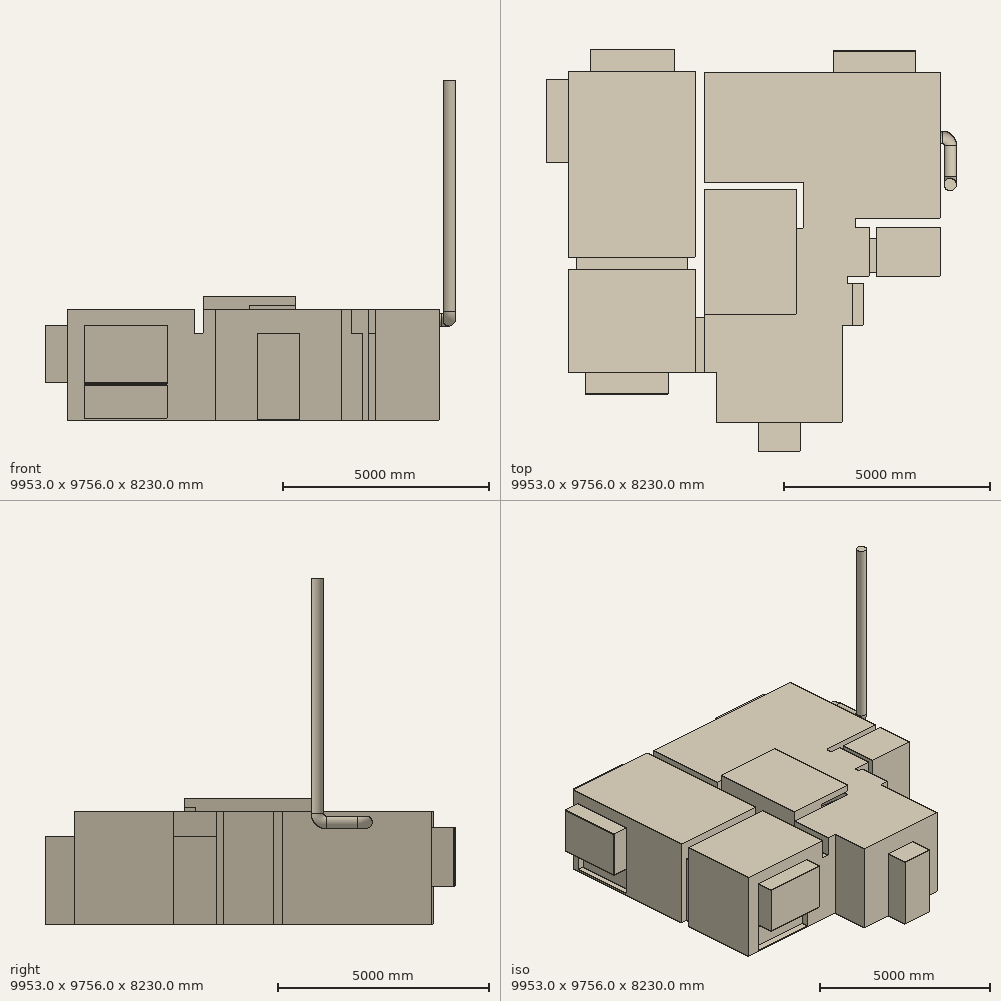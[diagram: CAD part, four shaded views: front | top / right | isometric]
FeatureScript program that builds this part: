
annotation { "Feature Type Name" : "Feature", "Feature Type Description" : "" }
export const myFeature = defineFeature(function(context is Context, id is Id, definition is map)
    precondition{}
    {
        {
            var Q0;
            Q0=qCreatedBy(makeId("Top.planeOp"),FACE);
            var sketch = newSketch(context, id + "F0", { "sketchPlane" : qUnion([Q0])});
            skLineSegment(sketch, "E0.bottom", {"start": v(-1549.14, 3434.73) * mm, "end": v(1546.86, 3434.73) * mm});
            skLineSegment(sketch, "E0.top", {"start": v(-1549.14, -1072.27) * mm, "end": v(1546.86, -1072.27) * mm});
            skLineSegment(sketch, "E0.left", {"start": v(-1549.14, 3434.73) * mm, "end": v(-1549.14, -1072.27) * mm});
            skLineSegment(sketch, "E0.right", {"start": v(1546.86, 3434.73) * mm, "end": v(1546.86, -1072.27) * mm});
            skSolve(sketch);
        }
        {
            var Q0;
            Q0=makeQuery(id+"F0.imprint","IMPRINT",FACE,{"disambiguationData":[TD([[makeQuery(id+"F0.imprint","IMPRINT",EDGE,{"derivedFrom":sQuery(id+"F0.wireOp",EDGE,"E0.bottom")}),-1.0]])]});
            extrude(context, id + "F1", {"entities" : qUnion([Q0]), "depth" : 2680 * mm});
        }
        {
            var Q0;
            Q0=makeQuery(id+"F1.opExtrude","SWEPT_FACE",FACE,{"disambiguationData":[OSD([sQuery(id+"F0.wireOp",EDGE,"E0.bottom")])]});
            var sketch = newSketch(context, id + "F2", { "sketchPlane" : qUnion([Q0])});
            skLineSegment(sketch, "E1.bottom", {"start": v(-1013.86, 2300) * mm, "end": v(1011.14, 2300) * mm});
            skLineSegment(sketch, "E1.top", {"start": v(-1013.86, 900) * mm, "end": v(1011.14, 900) * mm});
            skLineSegment(sketch, "E1.left", {"start": v(-1013.86, 2300) * mm, "end": v(-1013.86, 900) * mm});
            skLineSegment(sketch, "E1.right", {"start": v(1011.14, 2300) * mm, "end": v(1011.14, 900) * mm});
            skSolve(sketch);
        }
        {
            var Q0;
            Q0=qSketchRegion(id+"F2",true);
            extrude(context, id + "F3", {"entities" : qUnion([Q0]), "operationType" : NewBodyOperationType.ADD, "depth" : 532 * mm});
        }
        {
            var Q0;
            Q0=makeQuery(id+"F1.opExtrude","SWEPT_FACE",FACE,{"disambiguationData":[OSD([sQuery(id+"F0.wireOp",EDGE,"E0.left")])]});
            var sketch = newSketch(context, id + "F4", { "sketchPlane" : qUnion([Q0])});
            skLineSegment(sketch, "E2.bottom", {"start": v(-3238.73, 2300) * mm, "end": v(-1213.73, 2300) * mm});
            skLineSegment(sketch, "E2.top", {"start": v(-3238.73, 900) * mm, "end": v(-1213.73, 900) * mm});
            skLineSegment(sketch, "E2.left", {"start": v(-3238.73, 2300) * mm, "end": v(-3238.73, 900) * mm});
            skLineSegment(sketch, "E2.right", {"start": v(-1213.73, 2300) * mm, "end": v(-1213.73, 900) * mm});
            skSolve(sketch);
        }
        {
            var Q0;
            Q0=makeQuery(id+"F4.imprint","IMPRINT",FACE,{"disambiguationData":[TD([[makeQuery(id+"F4.imprint","IMPRINT",EDGE,{"derivedFrom":sQuery(id+"F4.wireOp",EDGE,"E2.bottom")}),-1.0]])]});
            extrude(context, id + "F5", {"entities" : qUnion([Q0]), "operationType" : NewBodyOperationType.ADD, "depth" : 532 * mm});
        }
        {
            var Q0;
            Q0=makeQuery(id+"F1.opExtrude","SWEPT_FACE",FACE,{"disambiguationData":[OSD([sQuery(id+"F0.wireOp",EDGE,"E0.bottom")])]});
            var sketch = newSketch(context, id + "F6", { "sketchPlane" : qUnion([Q0])});
            skLineSegment(sketch, "E3", {"start": v(1011.14, 900) * mm, "end": v(-1013.86, 900) * mm});
            skLineSegment(sketch, "E4.left", {"start": v(-1013.86, 835) * mm, "end": v(-1013.86, 35) * mm});
            skLineSegment(sketch, "E5.bottom", {"start": v(-1013.86, 835) * mm, "end": v(1011.14, 835) * mm});
            skLineSegment(sketch, "E5.top", {"start": v(-1013.86, 35) * mm, "end": v(1011.14, 35) * mm});
            skLineSegment(sketch, "E5.right", {"start": v(1011.14, 835) * mm, "end": v(1011.14, 35) * mm});
            skSolve(sketch);
        }
        {
            var Q0;
            Q0=makeQuery(id+"F6.imprint","IMPRINT",FACE,{"disambiguationData":[TD([[makeQuery(id+"F6.imprint","IMPRINT",EDGE,{"derivedFrom":sQuery(id+"F6.wireOp",EDGE,"E5.bottom")}),-1.0]])]});
            extrude(context, id + "F7", {"entities" : qUnion([Q0]), "operationType" : NewBodyOperationType.REMOVE, "oppositeDirection" : true, "depth" : 200 * mm});
        }
        {
            var Q0;
            Q0=makeQuery(id+"F1.opExtrude","CAP_FACE",FACE,{"disambiguationData":[OSD([sQuery(id+"F0.wireOp",EDGE,"E0.bottom"),sQuery(id+"F0.wireOp",EDGE,"E0.top"),sQuery(id+"F0.wireOp",EDGE,"E0.left"),sQuery(id+"F0.wireOp",EDGE,"E0.right")])],"isStart":true});
            var sketch = newSketch(context, id + "F8", { "sketchPlane" : qUnion([Q0])});
            skLineSegment(sketch, "E6", {"start": v(-1351.14, 1072.27) * mm, "end": v(-1351.14, 1375.27) * mm});
            skLineSegment(sketch, "E7", {"start": v(-1351.14, 1375.27) * mm, "end": v(1348.86, 1375.27) * mm});
            skLineSegment(sketch, "E8", {"start": v(1348.86, 1375.27) * mm, "end": v(1348.86, 1072.27) * mm});
            skLineSegment(sketch, "E9", {"start": v(1348.86, 1072.27) * mm, "end": v(-1351.14, 1072.27) * mm});
            skSolve(sketch);
        }
        {
            var Q0;
            Q0=makeQuery(id+"F8.imprint","IMPRINT",FACE,{"disambiguationData":[TD([[makeQuery(id+"F8.imprint","IMPRINT",EDGE,{"derivedFrom":sQuery(id+"F8.wireOp",EDGE,"E6")}),-1.0]])]});
            extrude(context, id + "F9", {"entities" : qUnion([Q0]), "operationType" : NewBodyOperationType.ADD, "oppositeDirection" : true, "depth" : 2100 * mm});
        }
        {
            var Q0;
            Q0=makeQuery(id+"F9.boolean.opBoolean","MERGE",FACE,{"derivedFrom":[makeQuery(id+"F1.opExtrude","CAP_FACE",FACE,{"disambiguationData":[OSD([sQuery(id+"F0.wireOp",EDGE,"E0.bottom"),sQuery(id+"F0.wireOp",EDGE,"E0.top"),sQuery(id+"F0.wireOp",EDGE,"E0.left"),sQuery(id+"F0.wireOp",EDGE,"E0.right")])],"isStart":true}),makeQuery(id+"F9.opExtrude","CAP_FACE",FACE,{"disambiguationData":[OSD([sQuery(id+"F8.wireOp",EDGE,"E6"),sQuery(id+"F8.wireOp",EDGE,"E7"),sQuery(id+"F8.wireOp",EDGE,"E8"),sQuery(id+"F8.wireOp",EDGE,"E9")])],"isStart":true})]});
            var sketch = newSketch(context, id + "F10", { "sketchPlane" : qUnion([Q0])});
            skLineSegment(sketch, "E10.bottom", {"start": v(-1549.14, 1375.27) * mm, "end": v(1546.86, 1375.27) * mm});
            skLineSegment(sketch, "E10.top", {"start": v(-1549.14, 3872.27) * mm, "end": v(1546.86, 3872.27) * mm});
            skLineSegment(sketch, "E10.left", {"start": v(-1549.14, 1375.27) * mm, "end": v(-1549.14, 3872.27) * mm});
            skLineSegment(sketch, "E10.right", {"start": v(1546.86, 1375.27) * mm, "end": v(1546.86, 3872.27) * mm});
            skLineSegment(sketch, "E11", {"start": v(-1549.14, 1375.27) * mm, "end": v(-1351.14, 1375.27) * mm});
            skSolve(sketch);
        }
        {
            var Q0;
            Q0=qSketchRegion(id+"F10",true);
            extrude(context, id + "F11", {"entities" : qUnion([Q0]), "operationType" : NewBodyOperationType.ADD, "oppositeDirection" : true, "depth" : 2680 * mm});
        }
        {
            var Q0;
            Q0=makeQuery(id+"F11.boolean.opBoolean","MERGE",FACE,{"derivedFrom":[makeQuery(id+"F9.boolean.opBoolean","MERGE",FACE,{"derivedFrom":[makeQuery(id+"F1.opExtrude","CAP_FACE",FACE,{"disambiguationData":[OSD([sQuery(id+"F0.wireOp",EDGE,"E0.bottom"),sQuery(id+"F0.wireOp",EDGE,"E0.top"),sQuery(id+"F0.wireOp",EDGE,"E0.left"),sQuery(id+"F0.wireOp",EDGE,"E0.right")])],"isStart":true}),makeQuery(id+"F9.opExtrude","CAP_FACE",FACE,{"disambiguationData":[OSD([sQuery(id+"F8.wireOp",EDGE,"E6"),sQuery(id+"F8.wireOp",EDGE,"E7"),sQuery(id+"F8.wireOp",EDGE,"E8"),sQuery(id+"F8.wireOp",EDGE,"E9")])],"isStart":true})]}),makeQuery(id+"F11.opExtrude","CAP_FACE",FACE,{"disambiguationData":[OSD([sQuery(id+"F10.wireOp",EDGE,"E10.bottom"),sQuery(id+"F10.wireOp",EDGE,"E10.top"),sQuery(id+"F10.wireOp",EDGE,"E10.left"),sQuery(id+"F10.wireOp",EDGE,"E10.right"),sQuery(id+"F10.wireOp",EDGE,"E11")])],"isStart":true})]});
            var sketch = newSketch(context, id + "F12", { "sketchPlane" : qUnion([Q0])});
            skLineSegment(sketch, "E12.bottom", {"start": v(1546.86, 3872.27) * mm, "end": v(1765.86, 3872.27) * mm});
            skLineSegment(sketch, "E12.top", {"start": v(1546.86, 2526.27) * mm, "end": v(1765.86, 2526.27) * mm});
            skLineSegment(sketch, "E12.left", {"start": v(1546.86, 3872.27) * mm, "end": v(1546.86, 2526.27) * mm});
            skLineSegment(sketch, "E12.right", {"start": v(1765.86, 3872.27) * mm, "end": v(1765.86, 2526.27) * mm});
            skSolve(sketch);
        }
        {
            var Q0;
            Q0=makeQuery(id+"F12.imprint","IMPRINT",FACE,{"disambiguationData":[TD([[makeQuery(id+"F12.imprint","IMPRINT",EDGE,{"derivedFrom":sQuery(id+"F12.wireOp",EDGE,"E12.bottom")}),-1.0]])]});
            extrude(context, id + "F13", {"entities" : qUnion([Q0]), "operationType" : NewBodyOperationType.ADD, "oppositeDirection" : true, "depth" : 2100 * mm});
        }
        {
            var Q0;
            Q0=makeQuery(id+"F13.boolean.opBoolean","MERGE",FACE,{"derivedFrom":[makeQuery(id+"F11.opExtrude","SWEPT_FACE",FACE,{"disambiguationData":[OSD([sQuery(id+"F10.wireOp",EDGE,"E10.top")])]}),makeQuery(id+"F13.opExtrude","SWEPT_FACE",FACE,{"disambiguationData":[OSD([sQuery(id+"F12.wireOp",EDGE,"E12.bottom")])]})]});
            var sketch = newSketch(context, id + "F14", { "sketchPlane" : qUnion([Q0])});
            skLineSegment(sketch, "E13.bottom", {"start": v(-1134.15, 2296.53) * mm, "end": v(890.85, 2296.53) * mm});
            skLineSegment(sketch, "E13.top", {"start": v(-1134.15, 896.53) * mm, "end": v(890.85, 896.53) * mm});
            skLineSegment(sketch, "E13.left", {"start": v(-1134.15, 2296.53) * mm, "end": v(-1134.15, 896.53) * mm});
            skLineSegment(sketch, "E13.right", {"start": v(890.85, 2296.53) * mm, "end": v(890.85, 896.53) * mm});
            skSolve(sketch);
        }
        {
            var Q0;
            Q0=makeQuery(id+"F14.imprint","IMPRINT",FACE,{"disambiguationData":[TD([[makeQuery(id+"F14.imprint","IMPRINT",EDGE,{"derivedFrom":sQuery(id+"F14.wireOp",EDGE,"E13.bottom")}),-1.0]])]});
            extrude(context, id + "F15", {"entities" : qUnion([Q0]), "operationType" : NewBodyOperationType.ADD, "depth" : 532 * mm});
        }
        {
            var Q0;
            Q0=makeQuery(id+"F12.imprint","IMPRINT",FACE,{"disambiguationData":[TD([[makeQuery(id+"F12.imprint","IMPRINT",EDGE,{"derivedFrom":sQuery(id+"F12.wireOp",EDGE,"E12.bottom")}),-1.0]])]});
            var sketch = newSketch(context, id + "F16", { "sketchPlane" : qUnion([Q0])});
            skLineSegment(sketch, "E14", {"start": v(1765.86, 3872.27) * mm, "end": v(2057.86, 3872.27) * mm});
            skLineSegment(sketch, "E15", {"start": v(2057.86, 3872.27) * mm, "end": v(2057.86, 5091.27) * mm});
            skLineSegment(sketch, "E16", {"start": v(1765.86, 3872.27) * mm, "end": v(1765.86, 2474.27) * mm});
            skLineSegment(sketch, "E17", {"start": v(1765.86, 2474.27) * mm, "end": v(2915.86, 2474.27) * mm});
            skLineSegment(sketch, "E18", {"start": v(2915.86, 2474.27) * mm, "end": v(2915.86, 2739.27) * mm});
            skLineSegment(sketch, "E19", {"start": v(2915.86, 2739.27) * mm, "end": v(5096.86, 2739.27) * mm});
            skLineSegment(sketch, "E20", {"start": v(5096.86, 2739.27) * mm, "end": v(5096.86, 5091.27) * mm});
            skLineSegment(sketch, "E21", {"start": v(2057.86, 5091.27) * mm, "end": v(5096.86, 5091.27) * mm});
            skSolve(sketch);
        }
        {
            var Q0;
            {var subQ1=sQuery(id+"F16.wireOp",EDGE,"E14");Q0=makeQuery(id+"F16.imprint","IMPRINT",FACE,{"disambiguationData":[TD([[makeQuery(id+"F16.imprint","IMPRINT",EDGE,{"derivedFrom":subQ1}),-1.0]])]});}
            extrude(context, id + "F17", {"entities" : qUnion([Q0]), "operationType" : NewBodyOperationType.ADD, "oppositeDirection" : true, "depth" : 2680 * mm});
        }
        {
            var Q0;
            Q0=makeQuery(id+"F17.boolean.opBoolean","MERGE",FACE,{"derivedFrom":[makeQuery(id+"F13.boolean.opBoolean","MERGE",FACE,{"derivedFrom":[makeQuery(id+"F11.boolean.opBoolean","MERGE",FACE,{"derivedFrom":[makeQuery(id+"F9.boolean.opBoolean","MERGE",FACE,{"derivedFrom":[makeQuery(id+"F1.opExtrude","CAP_FACE",FACE,{"disambiguationData":[OSD([sQuery(id+"F0.wireOp",EDGE,"E0.bottom"),sQuery(id+"F0.wireOp",EDGE,"E0.top"),sQuery(id+"F0.wireOp",EDGE,"E0.left"),sQuery(id+"F0.wireOp",EDGE,"E0.right")])],"isStart":true}),makeQuery(id+"F9.opExtrude","CAP_FACE",FACE,{"disambiguationData":[OSD([sQuery(id+"F8.wireOp",EDGE,"E6"),sQuery(id+"F8.wireOp",EDGE,"E7"),sQuery(id+"F8.wireOp",EDGE,"E8"),sQuery(id+"F8.wireOp",EDGE,"E9")])],"isStart":true})]}),makeQuery(id+"F11.opExtrude","CAP_FACE",FACE,{"disambiguationData":[OSD([sQuery(id+"F10.wireOp",EDGE,"E10.bottom"),sQuery(id+"F10.wireOp",EDGE,"E10.top"),sQuery(id+"F10.wireOp",EDGE,"E10.left"),sQuery(id+"F10.wireOp",EDGE,"E10.right"),sQuery(id+"F10.wireOp",EDGE,"E11")])],"isStart":true})]}),makeQuery(id+"F13.opExtrude","CAP_FACE",FACE,{"disambiguationData":[OSD([sQuery(id+"F12.wireOp",EDGE,"E12.bottom"),sQuery(id+"F12.wireOp",EDGE,"E12.top"),sQuery(id+"F12.wireOp",EDGE,"E12.left"),sQuery(id+"F12.wireOp",EDGE,"E12.right")])],"isStart":true})]}),makeQuery(id+"F17.opExtrude","CAP_FACE",FACE,{"disambiguationData":[OSD([sQuery(id+"F16.wireOp",EDGE,"E14"),sQuery(id+"F16.wireOp",EDGE,"E15"),sQuery(id+"F16.wireOp",EDGE,"E16"),sQuery(id+"F16.wireOp",EDGE,"E17"),sQuery(id+"F16.wireOp",EDGE,"E18"),sQuery(id+"F16.wireOp",EDGE,"E19"),sQuery(id+"F16.wireOp",EDGE,"E20"),sQuery(id+"F16.wireOp",EDGE,"E21")])],"isStart":true})]});
            var sketch = newSketch(context, id + "F18", { "sketchPlane" : qUnion([Q0])});
            skLineSegment(sketch, "E22.bottom", {"start": v(3064.86, 5091.27) * mm, "end": v(4089.86, 5091.27) * mm});
            skLineSegment(sketch, "E22.top", {"start": v(3064.86, 5789.27) * mm, "end": v(4089.86, 5789.27) * mm});
            skLineSegment(sketch, "E22.left", {"start": v(3064.86, 5091.27) * mm, "end": v(3064.86, 5789.27) * mm});
            skLineSegment(sketch, "E22.right", {"start": v(4089.86, 5091.27) * mm, "end": v(4089.86, 5789.27) * mm});
            skSolve(sketch);
        }
        {
            var Q0;
            Q0=makeQuery(id+"F18.imprint","IMPRINT",FACE,{"disambiguationData":[TD([[makeQuery(id+"F18.imprint","IMPRINT",EDGE,{"derivedFrom":sQuery(id+"F18.wireOp",EDGE,"E22.bottom")}),1.0]])]});
            extrude(context, id + "F19", {"entities" : qUnion([Q0]), "operationType" : NewBodyOperationType.ADD, "oppositeDirection" : true, "depth" : 2100 * mm});
        }
        {
            var Q0;
            {var subQ0=sQuery(id+"F16.wireOp",EDGE,"E14");Q0=makeQuery(id+"F16.imprint","IMPRINT",FACE,{"disambiguationData":[TD([[makeQuery(id+"F16.imprint","IMPRINT",EDGE,{"derivedFrom":subQ0}),-1.0]])]});}
            var sketch = newSketch(context, id + "F20", { "sketchPlane" : qUnion([Q0])});
            skLineSegment(sketch, "E23.bottom", {"start": v(1765.86, 2474.27) * mm, "end": v(3985.86, 2474.27) * mm});
            skLineSegment(sketch, "E23.top", {"start": v(1765.86, -565.73) * mm, "end": v(3985.86, -565.73) * mm});
            skLineSegment(sketch, "E23.left", {"start": v(1765.86, 2474.27) * mm, "end": v(1765.86, -565.73) * mm});
            skLineSegment(sketch, "E23.right", {"start": v(3985.86, 2474.27) * mm, "end": v(3985.86, -565.73) * mm});
            skSolve(sketch);
        }
        {
            var Q0;
            Q0=makeQuery(id+"F20.imprint","IMPRINT",FACE,{"disambiguationData":[TD([[makeQuery(id+"F20.imprint","IMPRINT",EDGE,{"derivedFrom":sQuery(id+"F20.wireOp",EDGE,"E23.top")}),1.0]])]});
            extrude(context, id + "F21", {"entities" : qUnion([Q0]), "oppositeDirection" : true, "depth" : 3000 * mm});
        }
        {
            var Q0;
            Q0=makeQuery(id+"F21.opExtrude","SWEPT_FACE",FACE,{"disambiguationData":[OSD([sQuery(id+"F20.wireOp",EDGE,"E23.left")])]});
            var sketch = newSketch(context, id + "F22", { "sketchPlane" : qUnion([Q0])});
            skLineSegment(sketch, "E24.MirrorCS", {"start": v(1199.27, 1020) * mm, "end": v(944.27, 1020) * mm});
            skLineSegment(sketch, "E25.MirrorCS", {"start": v(1709.27, 680) * mm, "end": v(1454.27, 680) * mm});
            skLineSegment(sketch, "E26.MirrorCS", {"start": v(2219.27, 340) * mm, "end": v(1964.27, 340) * mm});
            skLineSegment(sketch, "E27.MirrorCS", {"start": v(2474.27, 0) * mm, "end": v(2219.27, 0) * mm});
            skLineSegment(sketch, "E28.MirrorCS", {"start": v(1964.27, 340) * mm, "end": v(1964.27, 510) * mm});
            skLineSegment(sketch, "E29.MirrorCS", {"start": v(1454.27, 680) * mm, "end": v(1454.27, 850) * mm});
            skLineSegment(sketch, "E30.MirrorCS", {"start": v(1709.27, 510) * mm, "end": v(1709.27, 680) * mm});
            skLineSegment(sketch, "E31.MirrorCS", {"start": v(1199.27, 850) * mm, "end": v(1199.27, 1020) * mm});
            skLineSegment(sketch, "E32.MirrorCS", {"start": v(1454.27, 850) * mm, "end": v(1199.27, 850) * mm});
            skLineSegment(sketch, "E33.MirrorCS", {"start": v(-565.73, 1530) * mm, "end": v(-565.73, 1330) * mm});
            skLineSegment(sketch, "E34.MirrorCS", {"start": v(2219.27, 170) * mm, "end": v(2219.27, 340) * mm});
            skLineSegment(sketch, "E35.MirrorCS", {"start": v(2474.27, 170) * mm, "end": v(2219.27, 170) * mm});
            skLineSegment(sketch, "E36.MirrorCS", {"start": v(1964.27, 510) * mm, "end": v(1709.27, 510) * mm});
            skLineSegment(sketch, "E37.MirrorCS", {"start": v(2474.27, 0) * mm, "end": v(2474.27, 170) * mm});
            skLineSegment(sketch, "E38.MirrorCS", {"start": v(2474.27, 170) * mm, "end": v(2474.27, 0) * mm});
            skLineSegment(sketch, "E39", {"start": v(2219.27, 0) * mm, "end": v(179.27, 1330) * mm});
            skLineSegment(sketch, "E40", {"start": v(944.27, 1020) * mm, "end": v(944.27, 1190) * mm});
            skLineSegment(sketch, "E41", {"start": v(944.27, 1190) * mm, "end": v(689.27, 1190) * mm});
            skLineSegment(sketch, "E42", {"start": v(689.27, 1190) * mm, "end": v(689.27, 1330) * mm});
            skLineSegment(sketch, "E43", {"start": v(689.27, 1330) * mm, "end": v(434.27, 1330) * mm});
            skLineSegment(sketch, "E44", {"start": v(434.27, 1330) * mm, "end": v(434.27, 1530) * mm});
            skLineSegment(sketch, "E45", {"start": v(434.27, 1530) * mm, "end": v(-565.73, 1530) * mm});
            skLineSegment(sketch, "E46", {"start": v(-565.73, 1330) * mm, "end": v(179.27, 1330) * mm});
            skSolve(sketch);
        }
        {
            var Q0;
            Q0=qSketchRegion(id+"F22",true);
            extrude(context, id + "F23", {"entities" : qUnion([Q0]), "operationType" : NewBodyOperationType.REMOVE, "oppositeDirection" : true, "depth" : 1110 * mm});
        }
        {
            var Q0;
            Q0=makeQuery(id+"F21.opExtrude","SWEPT_FACE",FACE,{"disambiguationData":[OSD([sQuery(id+"F20.wireOp",EDGE,"E23.right")])]});
            var sketch = newSketch(context, id + "F24", { "sketchPlane" : qUnion([Q0])});
            skLineSegment(sketch, "E47", {"start": v(565.73, 1530) * mm, "end": v(-689.27, 1530) * mm});
            skLineSegment(sketch, "E48", {"start": v(-689.27, 1530) * mm, "end": v(-689.27, 1710) * mm});
            skLineSegment(sketch, "E49", {"start": v(-689.27, 1710) * mm, "end": v(-944.27, 1710) * mm});
            skLineSegment(sketch, "E50", {"start": v(-944.27, 1710) * mm, "end": v(-944.27, 1890) * mm});
            skLineSegment(sketch, "E51", {"start": v(-944.27, 1890) * mm, "end": v(-1199.27, 1890) * mm});
            skLineSegment(sketch, "E52", {"start": v(-1199.27, 1890) * mm, "end": v(-1199.27, 2070) * mm});
            skLineSegment(sketch, "E53", {"start": v(-1199.27, 2070) * mm, "end": v(-1454.27, 2070) * mm});
            skLineSegment(sketch, "E54", {"start": v(-1454.27, 2070) * mm, "end": v(-1454.27, 2250) * mm});
            skLineSegment(sketch, "E55", {"start": v(-1454.27, 2250) * mm, "end": v(-1709.27, 2250) * mm});
            skLineSegment(sketch, "E56", {"start": v(-1709.27, 2430) * mm, "end": v(-1709.27, 2250) * mm});
            skLineSegment(sketch, "E57", {"start": v(565.73, 1530) * mm, "end": v(565.73, 1330) * mm});
            skLineSegment(sketch, "E58", {"start": v(-689.27, 1330) * mm, "end": v(565.73, 1330) * mm});
            skLineSegment(sketch, "E59", {"start": v(-1709.27, 2430) * mm, "end": v(-1964.27, 2430) * mm});
            skLineSegment(sketch, "E60", {"start": v(-1964.27, 2430) * mm, "end": v(-1964.27, 2610) * mm});
            skLineSegment(sketch, "E61", {"start": v(-1964.27, 2610) * mm, "end": v(-2219.27, 2610) * mm});
            skLineSegment(sketch, "E62", {"start": v(-2219.27, 2610) * mm, "end": v(-2219.27, 2790) * mm});
            skLineSegment(sketch, "E63", {"start": v(-2219.27, 2790) * mm, "end": v(-2474.27, 2790) * mm});
            skLineSegment(sketch, "E64", {"start": v(-2474.27, 2651.89) * mm, "end": v(-689.27, 1330) * mm});
            skLineSegment(sketch, "E65", {"start": v(-2474.27, 2651.89) * mm, "end": v(-2474.27, 2790) * mm});
            skLineSegment(sketch, "E66", {"start": v(565.73, 1330) * mm, "end": v(565.73, 1530) * mm});
            skLineSegment(sketch, "E67", {"start": v(-689.27, 1530) * mm, "end": v(565.73, 1530) * mm});
            skSolve(sketch);
        }
        {
            var Q0;
            Q0=makeQuery(id+"F24.imprint","IMPRINT",FACE,{"disambiguationData":[TD([[makeQuery(id+"F24.imprint","IMPRINT",EDGE,{"derivedFrom":sQuery(id+"F24.wireOp",EDGE,"E48")}),1.0]])]});
            extrude(context, id + "F25", {"entities" : qUnion([Q0]), "operationType" : NewBodyOperationType.REMOVE, "oppositeDirection" : true, "depth" : 1120 * mm});
        }
        {
            var Q0;
            Q0=makeQuery(id+"F17.opExtrude","CAP_FACE",FACE,{"disambiguationData":[OSD([sQuery(id+"F16.wireOp",EDGE,"E14"),sQuery(id+"F16.wireOp",EDGE,"E15"),sQuery(id+"F16.wireOp",EDGE,"E16"),sQuery(id+"F16.wireOp",EDGE,"E17"),sQuery(id+"F16.wireOp",EDGE,"E18"),sQuery(id+"F16.wireOp",EDGE,"E19"),sQuery(id+"F16.wireOp",EDGE,"E20"),sQuery(id+"F16.wireOp",EDGE,"E21")])],"isStart":false});
            var sketch = newSketch(context, id + "F26", { "sketchPlane" : qUnion([Q0])});
            skLineSegment(sketch, "E68", {"start": v(5096.86, -2739.27) * mm, "end": v(5356.86, -2739.27) * mm});
            skLineSegment(sketch, "E69", {"start": v(5221.86, -1714.27) * mm, "end": v(5221.86, -1554.27) * mm});
            skLineSegment(sketch, "E70", {"start": v(5221.86, -1554.27) * mm, "end": v(5771.86, -1554.27) * mm});
            skLineSegment(sketch, "E71", {"start": v(5771.86, -1554.27) * mm, "end": v(5771.86, -1454.27) * mm});
            skLineSegment(sketch, "E72", {"start": v(5771.86, -629.27) * mm, "end": v(5771.86, -354.27) * mm});
            skLineSegment(sketch, "E73", {"start": v(5771.86, -354.27) * mm, "end": v(5421.86, -354.27) * mm});
            skLineSegment(sketch, "E74", {"start": v(5421.86, -354.27) * mm, "end": v(5421.86, -142.27) * mm});
            skLineSegment(sketch, "E75", {"start": v(7471.86, 3404.73) * mm, "end": v(6893.86, 3404.73) * mm});
            skLineSegment(sketch, "E76", {"start": v(4681.86, 3404.73) * mm, "end": v(1765.86, 3404.73) * mm});
            skLineSegment(sketch, "E77", {"start": v(1765.86, 3404.73) * mm, "end": v(1765.86, 747.73) * mm});
            skLineSegment(sketch, "E78", {"start": v(1765.86, 747.73) * mm, "end": v(4146.86, 747.73) * mm});
            skLineSegment(sketch, "E79", {"start": v(4146.86, 747.73) * mm, "end": v(4146.86, -384.27) * mm});
            skLineSegment(sketch, "E80", {"start": v(5096.86, -2739.27) * mm, "end": v(2915.86, -2739.27) * mm});
            skLineSegment(sketch, "E81", {"start": v(2915.86, -2739.27) * mm, "end": v(2915.86, -2474.27) * mm});
            skLineSegment(sketch, "E82", {"start": v(2915.86, -2474.27) * mm, "end": v(3985.86, -2474.27) * mm});
            skLineSegment(sketch, "E83", {"start": v(3985.86, -2474.27) * mm, "end": v(3985.86, -384.27) * mm});
            skLineSegment(sketch, "E84", {"start": v(3985.86, -384.27) * mm, "end": v(4146.86, -384.27) * mm});
            skLineSegment(sketch, "E85", {"start": v(5771.86, -629.27) * mm, "end": v(5771.86, -1454.27) * mm});
            skLineSegment(sketch, "E86", {"start": v(4681.86, 3404.73) * mm, "end": v(6893.86, 3404.73) * mm});
            skLineSegment(sketch, "E87", {"start": v(5356.86, -2739.27) * mm, "end": v(5356.86, -1714.27) * mm});
            skLineSegment(sketch, "E88", {"start": v(5356.86, -1714.27) * mm, "end": v(5221.86, -1714.27) * mm});
            skLineSegment(sketch, "E89", {"start": v(7471.86, 3404.73) * mm, "end": v(7471.86, -142.27) * mm});
            skLineSegment(sketch, "E90", {"start": v(5421.86, -142.27) * mm, "end": v(7471.86, -142.27) * mm});
            skSolve(sketch);
        }
        {
            var Q0;
            Q0=makeQuery(id+"F26.imprint","IMPRINT",FACE,{"disambiguationData":[TD([[makeQuery(id+"F26.imprint","IMPRINT",EDGE,{"derivedFrom":sQuery(id+"F26.wireOp",EDGE,"E68")}),1.0]])]});
            extrude(context, id + "F27", {"entities" : qUnion([Q0]), "oppositeDirection" : true, "depth" : 2680 * mm});
        }
        {
            var Q0;
            Q0=makeQuery(id+"F27.opExtrude","SWEPT_FACE",FACE,{"disambiguationData":[OSD([sQuery(id+"F26.wireOp",EDGE,"E75"),sQuery(id+"F26.wireOp",EDGE,"E76"),sQuery(id+"F26.wireOp",EDGE,"E86")])]});
            var sketch = newSketch(context, id + "F28", { "sketchPlane" : qUnion([Q0])});
            skLineSegment(sketch, "E91.bottom", {"start": v(-6883.86, 2300) * mm, "end": v(-4883.86, 2300) * mm});
            skLineSegment(sketch, "E91.top", {"start": v(-6883.86, 900) * mm, "end": v(-4883.86, 900) * mm});
            skLineSegment(sketch, "E91.left", {"start": v(-6883.86, 2300) * mm, "end": v(-6883.86, 900) * mm});
            skLineSegment(sketch, "E91.right", {"start": v(-4883.86, 2300) * mm, "end": v(-4883.86, 900) * mm});
            skSolve(sketch);
        }
        {
            var Q0;
            Q0=makeQuery(id+"F28.imprint","IMPRINT",FACE,{"disambiguationData":[TD([[makeQuery(id+"F28.imprint","IMPRINT",EDGE,{"derivedFrom":sQuery(id+"F28.wireOp",EDGE,"E91.bottom")}),-1.0]])]});
            extrude(context, id + "F29", {"entities" : qUnion([Q0]), "operationType" : NewBodyOperationType.ADD, "depth" : 532 * mm});
        }
        {
            var Q0;
            Q0=makeQuery(id+"F27.opExtrude","SWEPT_FACE",FACE,{"disambiguationData":[OSD([sQuery(id+"F26.wireOp",EDGE,"E71"),sQuery(id+"F26.wireOp",EDGE,"E72"),sQuery(id+"F26.wireOp",EDGE,"E85")])]});
            var sketch = newSketch(context, id + "F30", { "sketchPlane" : qUnion([Q0])});
            skLineSegment(sketch, "E92.bottom", {"start": v(-1454.27, 2100) * mm, "end": v(-629.27, 2100) * mm});
            skLineSegment(sketch, "E92.top", {"start": v(-1454.27, 0) * mm, "end": v(-629.27, 0) * mm});
            skLineSegment(sketch, "E92.left", {"start": v(-1454.27, 2100) * mm, "end": v(-1454.27, 0) * mm});
            skLineSegment(sketch, "E92.right", {"start": v(-629.27, 2100) * mm, "end": v(-629.27, 0) * mm});
            skSolve(sketch);
        }
        {
            var Q0;
            Q0=makeQuery(id+"F30.imprint","IMPRINT",FACE,{"disambiguationData":[TD([[makeQuery(id+"F30.imprint","IMPRINT",EDGE,{"derivedFrom":sQuery(id+"F30.wireOp",EDGE,"E92.bottom")}),-1.0]])]});
            extrude(context, id + "F31", {"entities" : qUnion([Q0]), "operationType" : NewBodyOperationType.ADD, "depth" : 160 * mm});
        }
        {
            var Q0;
            Q0=makeQuery(id+"F31.opExtrude","CAP_FACE",FACE,{"disambiguationData":[OSD([sQuery(id+"F30.wireOp",EDGE,"E92.bottom"),sQuery(id+"F30.wireOp",EDGE,"E92.top"),sQuery(id+"F30.wireOp",EDGE,"E92.left"),sQuery(id+"F30.wireOp",EDGE,"E92.right")])],"isStart":false});
            var sketch = newSketch(context, id + "F32", { "sketchPlane" : qUnion([Q0])});
            skLineSegment(sketch, "E93.bottom", {"start": v(-1554.27, 2680) * mm, "end": v(-354.27, 2680) * mm});
            skLineSegment(sketch, "E93.top", {"start": v(-1554.27, 0) * mm, "end": v(-354.27, 0) * mm});
            skLineSegment(sketch, "E93.left", {"start": v(-1554.27, 2680) * mm, "end": v(-1554.27, 0) * mm});
            skLineSegment(sketch, "E93.right", {"start": v(-354.27, 2680) * mm, "end": v(-354.27, 0) * mm});
            skSolve(sketch);
        }
        {
            var Q0;
            Q0=qSketchRegion(id+"F32",true);
            extrude(context, id + "F33", {"entities" : qUnion([Q0]), "operationType" : NewBodyOperationType.ADD, "depth" : 1540 * mm});
        }
        {
            var Q0;
            Q0=makeQuery(id+"F1.opExtrude","SWEPT_BODY",BODY,{"disambiguationData":[OSD([sQuery(id+"F0.wireOp",EDGE,"E0.bottom"),sQuery(id+"F0.wireOp",EDGE,"E0.top"),sQuery(id+"F0.wireOp",EDGE,"E0.left"),sQuery(id+"F0.wireOp",EDGE,"E0.right")])]});
            var Q1;
            Q1=makeQuery(id+"F27.opExtrude","SWEPT_BODY",BODY,{"disambiguationData":[OSD([sQuery(id+"F26.wireOp",EDGE,"E68"),sQuery(id+"F26.wireOp",EDGE,"f08b4c50-08dc-44d1-91bd-df31dd3f817a"),sQuery(id+"F26.wireOp",EDGE,"f896f5a7-1bc8-498b-a9e9-afe6711b9f40"),sQuery(id+"F26.wireOp",EDGE,"E69"),sQuery(id+"F26.wireOp",EDGE,"E70"),sQuery(id+"F26.wireOp",EDGE,"E71"),sQuery(id+"F26.wireOp",EDGE,"E72"),sQuery(id+"F26.wireOp",EDGE,"E73"),sQuery(id+"F26.wireOp",EDGE,"E74"),sQuery(id+"F26.wireOp",EDGE,"4dea9934-df3e-44db-ac8b-cfe9eaf94726"),sQuery(id+"F26.wireOp",EDGE,"69e68077-ab11-4f7d-8ed4-810636c2d2b1"),sQuery(id+"F26.wireOp",EDGE,"E75"),sQuery(id+"F26.wireOp",EDGE,"E76"),sQuery(id+"F26.wireOp",EDGE,"E77"),sQuery(id+"F26.wireOp",EDGE,"E78"),sQuery(id+"F26.wireOp",EDGE,"E79"),sQuery(id+"F26.wireOp",EDGE,"E80"),sQuery(id+"F26.wireOp",EDGE,"E81"),sQuery(id+"F26.wireOp",EDGE,"E82"),sQuery(id+"F26.wireOp",EDGE,"E83"),sQuery(id+"F26.wireOp",EDGE,"E84"),sQuery(id+"F26.wireOp",EDGE,"de4f6d5e-2732-43ff-8072-bc847a33fe50"),sQuery(id+"F26.wireOp",EDGE,"2b71e373-8316-4eaa-b8c1-09a88fac9cdd"),sQuery(id+"F26.wireOp",EDGE,"9742d433-c769-4375-8eee-a89ad4486bd9"),sQuery(id+"F26.wireOp",EDGE,"E85"),sQuery(id+"F26.wireOp",EDGE,"E86")])]});
            booleanBodies(context, id + "F34", {"operationType" : BooleanOperationType.UNION, "tools" : qUnion([Q0, Q1])});
        }
        {
            var Q0;
            Q0=makeQuery(id+"F21.opExtrude","CAP_FACE",FACE,{"disambiguationData":[OSD([sQuery(id+"F20.wireOp",EDGE,"E23.bottom"),sQuery(id+"F20.wireOp",EDGE,"E23.top"),sQuery(id+"F20.wireOp",EDGE,"E23.left"),sQuery(id+"F20.wireOp",EDGE,"E23.right")])],"isStart":false});
            var sketch = newSketch(context, id + "F35", { "sketchPlane" : qUnion([Q0])});
            skSolve(sketch);
        }
        {
            var Q0;
            Q0=makeQuery(id+"F27.opExtrude","SWEPT_FACE",FACE,{"disambiguationData":[OSD([sQuery(id+"F26.wireOp",EDGE,"E87")])]});
            var sketch = newSketch(context, id + "F36", { "sketchPlane" : qUnion([Q0])});
            skLineSegment(sketch, "E94.bottom", {"start": v(-2739.27, 0) * mm, "end": v(-1714.27, 0) * mm});
            skLineSegment(sketch, "E94.top", {"start": v(-2739.27, 2100) * mm, "end": v(-1714.27, 2100) * mm});
            skLineSegment(sketch, "E94.left", {"start": v(-2739.27, 0) * mm, "end": v(-2739.27, 2100) * mm});
            skLineSegment(sketch, "E94.right", {"start": v(-1714.27, 0) * mm, "end": v(-1714.27, 2100) * mm});
            skSolve(sketch);
        }
        {
            var Q0;
            Q0=makeQuery(id+"F36.imprint","IMPRINT",FACE,{"disambiguationData":[TD([[makeQuery(id+"F36.imprint","IMPRINT",EDGE,{"derivedFrom":sQuery(id+"F36.wireOp",EDGE,"E94.bottom")}),1.0]])]});
            extrude(context, id + "F37", {"entities" : qUnion([Q0]), "operationType" : NewBodyOperationType.ADD, "depth" : 260 * mm});
        }
        {
            var Q0;
            Q0=makeQuery(id+"F3.opExtrude","CAP_EDGE",EDGE,{"disambiguationData":[OSD([sQuery(id+"F2.wireOp",EDGE,"E1.top")])],"isStart":false});
            chamfer(context, id + "F38", {"entities" : qUnion([Q0]), "width" : 10 * mm, "tangentPropagation" : true});
        }
        {
            var Q0;
            Q0=makeQuery(id+"F19.opExtrude","CAP_EDGE",EDGE,{"disambiguationData":[OSD([sQuery(id+"F18.wireOp",EDGE,"E22.top")])],"isStart":true});
            chamfer(context, id + "F39", {"entities" : qUnion([Q0]), "width" : 10 * mm, "tangentPropagation" : true});
        }
        {
            var Q0;
            Q0=makeQuery(id+"F1.opExtrude","SWEPT_FACE",FACE,{"disambiguationData":[OSD([sQuery(id+"F0.wireOp",EDGE,"E0.left")])]});
            var sketch = newSketch(context, id + "F40", { "sketchPlane" : qUnion([Q0])});
            skLineSegment(sketch, "E95.left", {"start": v(-3238.73, 860) * mm, "end": v(-3238.73, 60) * mm});
            skLineSegment(sketch, "E96.bottom", {"start": v(-3238.73, 860) * mm, "end": v(-1213.73, 860) * mm});
            skLineSegment(sketch, "E96.top", {"start": v(-3238.73, 60) * mm, "end": v(-1213.73, 60) * mm});
            skLineSegment(sketch, "E96.right", {"start": v(-1213.73, 860) * mm, "end": v(-1213.73, 60) * mm});
            skSolve(sketch);
        }
        {
            var Q0;
            Q0=makeQuery(id+"FUjL85pzEbzD5bS_4.opExtrude","CAP_EDGE",EDGE,{"disambiguationData":[OSD([sQuery(id+"FVQUxZKEPlPMTY7_4.wireOp",EDGE,"27f17da1-5a32-4777-b596-18b2b9e2d772.top")])],"isStart":false});
            var Q1;
            Q1=makeQuery(id+"F96XkMD0H0Lt718_4.opExtrude","CAP_EDGE",EDGE,{"disambiguationData":[OSD([sQuery(id+"FRb6ArTOglKZPxY_4.wireOp",EDGE,"a2c4a1ad-d57d-4a5c-ab78-e5cd951a2702.top")])],"isStart":false});
            var Q2;
            Q2=makeQuery(id+"F15.opExtrude","CAP_EDGE",EDGE,{"disambiguationData":[OSD([sQuery(id+"F14.wireOp",EDGE,"E13.top")])],"isStart":false});
            var Q3;
            Q3=makeQuery(id+"FYTNxJxaLjeZUNO_3.opExtrude","CAP_EDGE",EDGE,{"disambiguationData":[OSD([sQuery(id+"FuwheIhAnHBxXwV_3.wireOp",EDGE,"38c65481-2646-4b2d-9396-5d1f6ef7d6af.top")])],"isStart":false});
            var Q4;
            Q4=makeQuery(id+"F5.opExtrude","CAP_EDGE",EDGE,{"disambiguationData":[OSD([sQuery(id+"F4.wireOp",EDGE,"E2.top")])],"isStart":false});
            var Q5;
            Q5=makeQuery(id+"FoKxzR6qpxnYhbw_3.opExtrude","CAP_EDGE",EDGE,{"disambiguationData":[OSD([sQuery(id+"Fxmn0H0jBOv929n_3.wireOp",EDGE,"2744b7c8-5e17-4509-a646-23f99c13ef3b.top")])],"isStart":false});
            var Q6;
            Q6=makeQuery(id+"FFo818rkfokuCDJ_3.opExtrude","CAP_EDGE",EDGE,{"disambiguationData":[OSD([sQuery(id+"FEg9MHS8PfZ1KpK_3.wireOp",EDGE,"9deabb99-1272-497d-a1d5-82df617a77d8.top")])],"isStart":false});
            var Q7;
            Q7=makeQuery(id+"F29.opExtrude","CAP_EDGE",EDGE,{"disambiguationData":[OSD([sQuery(id+"F28.wireOp",EDGE,"E91.top")])],"isStart":false});
            var Q8;
            Q8=makeQuery(id+"F37.opExtrude","CAP_EDGE",EDGE,{"disambiguationData":[OSD([sQuery(id+"F36.wireOp",EDGE,"E94.bottom")])],"isStart":false});
            var Q9;
            Q9=makeQuery(id+"FUjL85pzEbzD5bS_4.opExtrude","CAP_EDGE",EDGE,{"disambiguationData":[OSD([sQuery(id+"FVQUxZKEPlPMTY7_4.wireOp",EDGE,"27f17da1-5a32-4777-b596-18b2b9e2d772.left")])],"isStart":false});
            var Q10;
            Q10=makeQuery(id+"FUjL85pzEbzD5bS_4.opExtrude","CAP_EDGE",EDGE,{"disambiguationData":[OSD([sQuery(id+"FVQUxZKEPlPMTY7_4.wireOp",EDGE,"27f17da1-5a32-4777-b596-18b2b9e2d772.right")])],"isStart":false});
            var Q11;
            Q11=makeQuery(id+"FUjL85pzEbzD5bS_4.opExtrude","CAP_EDGE",EDGE,{"disambiguationData":[OSD([sQuery(id+"FVQUxZKEPlPMTY7_4.wireOp",EDGE,"27f17da1-5a32-4777-b596-18b2b9e2d772.bottom")])],"isStart":false});
            var Q12;
            Q12=makeQuery(id+"F96XkMD0H0Lt718_4.opExtrude","CAP_EDGE",EDGE,{"disambiguationData":[OSD([sQuery(id+"FRb6ArTOglKZPxY_4.wireOp",EDGE,"a2c4a1ad-d57d-4a5c-ab78-e5cd951a2702.left")])],"isStart":false});
            var Q13;
            Q13=makeQuery(id+"F96XkMD0H0Lt718_4.opExtrude","CAP_EDGE",EDGE,{"disambiguationData":[OSD([sQuery(id+"FRb6ArTOglKZPxY_4.wireOp",EDGE,"a2c4a1ad-d57d-4a5c-ab78-e5cd951a2702.bottom")])],"isStart":false});
            var Q14;
            Q14=makeQuery(id+"F96XkMD0H0Lt718_4.opExtrude","CAP_EDGE",EDGE,{"disambiguationData":[OSD([sQuery(id+"FRb6ArTOglKZPxY_4.wireOp",EDGE,"a2c4a1ad-d57d-4a5c-ab78-e5cd951a2702.right")])],"isStart":false});
            var Q15;
            Q15=makeQuery(id+"F15.opExtrude","CAP_EDGE",EDGE,{"disambiguationData":[OSD([sQuery(id+"F14.wireOp",EDGE,"E13.left")])],"isStart":false});
            var Q16;
            Q16=makeQuery(id+"F15.opExtrude","CAP_EDGE",EDGE,{"disambiguationData":[OSD([sQuery(id+"F14.wireOp",EDGE,"E13.bottom")])],"isStart":false});
            var Q17;
            Q17=makeQuery(id+"F15.opExtrude","CAP_EDGE",EDGE,{"disambiguationData":[OSD([sQuery(id+"F14.wireOp",EDGE,"E13.right")])],"isStart":false});
            var Q18;
            Q18=makeQuery(id+"F5.opExtrude","CAP_EDGE",EDGE,{"disambiguationData":[OSD([sQuery(id+"F4.wireOp",EDGE,"E2.bottom")])],"isStart":false});
            var Q19;
            Q19=makeQuery(id+"F5.opExtrude","CAP_EDGE",EDGE,{"disambiguationData":[OSD([sQuery(id+"F4.wireOp",EDGE,"E2.right")])],"isStart":false});
            var Q20;
            Q20=makeQuery(id+"F5.opExtrude","CAP_EDGE",EDGE,{"disambiguationData":[OSD([sQuery(id+"F4.wireOp",EDGE,"E2.left")])],"isStart":false});
            var Q21;
            Q21=makeQuery(id+"FYTNxJxaLjeZUNO_3.opExtrude","CAP_EDGE",EDGE,{"disambiguationData":[OSD([sQuery(id+"FuwheIhAnHBxXwV_3.wireOp",EDGE,"38c65481-2646-4b2d-9396-5d1f6ef7d6af.left")])],"isStart":false});
            var Q22;
            Q22=makeQuery(id+"FYTNxJxaLjeZUNO_3.opExtrude","CAP_EDGE",EDGE,{"disambiguationData":[OSD([sQuery(id+"FuwheIhAnHBxXwV_3.wireOp",EDGE,"38c65481-2646-4b2d-9396-5d1f6ef7d6af.bottom")])],"isStart":false});
            var Q23;
            Q23=makeQuery(id+"FYTNxJxaLjeZUNO_3.opExtrude","CAP_EDGE",EDGE,{"disambiguationData":[OSD([sQuery(id+"FuwheIhAnHBxXwV_3.wireOp",EDGE,"38c65481-2646-4b2d-9396-5d1f6ef7d6af.right")])],"isStart":false});
            var Q24;
            Q24=makeQuery(id+"F3.opExtrude","CAP_EDGE",EDGE,{"disambiguationData":[OSD([sQuery(id+"F2.wireOp",EDGE,"E1.bottom")])],"isStart":false});
            var Q25;
            Q25=makeQuery(id+"F3.opExtrude","CAP_EDGE",EDGE,{"disambiguationData":[OSD([sQuery(id+"F2.wireOp",EDGE,"E1.left")])],"isStart":false});
            var Q26;
            Q26=makeQuery(id+"F3.opExtrude","CAP_EDGE",EDGE,{"disambiguationData":[OSD([sQuery(id+"F2.wireOp",EDGE,"E1.right")])],"isStart":false});
            var Q27;
            {var subQ0=sQuery(id+"F2.wireOp",EDGE,"E1.top");Q27=makeQuery(id+"F38.opChamfer","BLEND_EDGE",EDGE,{"blendedFrom":[makeQuery(id+"F3.opExtrude","CAP_EDGE",EDGE,{"disambiguationData":[OSD([subQ0])],"isStart":false}),makeQuery(id+"F3.opExtrude","CAP_FACE",FACE,{"disambiguationData":[OSD([sQuery(id+"F2.wireOp",EDGE,"E1.bottom"),subQ0,sQuery(id+"F2.wireOp",EDGE,"E1.left"),sQuery(id+"F2.wireOp",EDGE,"E1.right")])],"isStart":false})],"blendedInto":[makeQuery(id+"F3.opExtrude","CAP_FACE",FACE,{"disambiguationData":[OSD([sQuery(id+"F2.wireOp",EDGE,"E1.bottom"),subQ0,sQuery(id+"F2.wireOp",EDGE,"E1.left"),sQuery(id+"F2.wireOp",EDGE,"E1.right")])],"isStart":false})]});}
            var Q28;
            Q28=makeQuery(id+"FFo818rkfokuCDJ_3.opExtrude","CAP_EDGE",EDGE,{"disambiguationData":[OSD([sQuery(id+"FEg9MHS8PfZ1KpK_3.wireOp",EDGE,"9deabb99-1272-497d-a1d5-82df617a77d8.left")])],"isStart":false});
            var Q29;
            Q29=makeQuery(id+"FFo818rkfokuCDJ_3.opExtrude","CAP_EDGE",EDGE,{"disambiguationData":[OSD([sQuery(id+"FEg9MHS8PfZ1KpK_3.wireOp",EDGE,"9deabb99-1272-497d-a1d5-82df617a77d8.right")])],"isStart":false});
            var Q30;
            Q30=makeQuery(id+"FFo818rkfokuCDJ_3.opExtrude","CAP_EDGE",EDGE,{"disambiguationData":[OSD([sQuery(id+"FEg9MHS8PfZ1KpK_3.wireOp",EDGE,"9deabb99-1272-497d-a1d5-82df617a77d8.bottom")])],"isStart":false});
            var Q31;
            Q31=makeQuery(id+"FoKxzR6qpxnYhbw_3.opExtrude","CAP_EDGE",EDGE,{"disambiguationData":[OSD([sQuery(id+"Fxmn0H0jBOv929n_3.wireOp",EDGE,"2744b7c8-5e17-4509-a646-23f99c13ef3b.bottom")])],"isStart":false});
            var Q32;
            Q32=makeQuery(id+"FoKxzR6qpxnYhbw_3.opExtrude","CAP_EDGE",EDGE,{"disambiguationData":[OSD([sQuery(id+"Fxmn0H0jBOv929n_3.wireOp",EDGE,"2744b7c8-5e17-4509-a646-23f99c13ef3b.right")])],"isStart":false});
            var Q33;
            Q33=makeQuery(id+"FoKxzR6qpxnYhbw_3.opExtrude","CAP_EDGE",EDGE,{"disambiguationData":[OSD([sQuery(id+"Fxmn0H0jBOv929n_3.wireOp",EDGE,"2744b7c8-5e17-4509-a646-23f99c13ef3b.left")])],"isStart":false});
            var Q34;
            Q34=makeQuery(id+"F29.opExtrude","CAP_EDGE",EDGE,{"disambiguationData":[OSD([sQuery(id+"F28.wireOp",EDGE,"E91.right")])],"isStart":false});
            var Q35;
            Q35=makeQuery(id+"F29.opExtrude","CAP_EDGE",EDGE,{"disambiguationData":[OSD([sQuery(id+"F28.wireOp",EDGE,"E91.bottom")])],"isStart":false});
            var Q36;
            Q36=makeQuery(id+"F29.opExtrude","CAP_EDGE",EDGE,{"disambiguationData":[OSD([sQuery(id+"F28.wireOp",EDGE,"E91.left")])],"isStart":false});
            var Q37;
            Q37=makeQuery(id+"FqoP4yYfcrjL1BX_4.opExtrude","CAP_EDGE",EDGE,{"disambiguationData":[OSD([sQuery(id+"FZ26vsHNQvjIOnw_4.wireOp",EDGE,"912f45f2-db5d-419c-a15d-ae6ab1006993.bottom")])],"isStart":false});
            var Q38;
            Q38=makeQuery(id+"FPQ3s8IO0Nq6tfT_4.opExtrude","CAP_EDGE",EDGE,{"disambiguationData":[OSD([sQuery(id+"Fhg7J0d2X8vjHtq_4.wireOp",EDGE,"c37dfdb1-f1d7-45b2-8367-4b2e48f77e16.bottom")])],"isStart":false});
            var Q39;
            Q39=makeQuery(id+"FPQ3s8IO0Nq6tfT_4.opExtrude","CAP_EDGE",EDGE,{"disambiguationData":[OSD([sQuery(id+"Fhg7J0d2X8vjHtq_4.wireOp",EDGE,"c37dfdb1-f1d7-45b2-8367-4b2e48f77e16.right")])],"isStart":false});
            var Q40;
            {var subQ0=sQuery(id+"Fhg7J0d2X8vjHtq_4.wireOp",EDGE,"c37dfdb1-f1d7-45b2-8367-4b2e48f77e16.top");Q40=makeQuery(id+"FNpFcnb2nyaKgwG_1.opChamfer","BLEND_EDGE",EDGE,{"blendedFrom":[makeQuery(id+"FPQ3s8IO0Nq6tfT_4.opExtrude","CAP_EDGE",EDGE,{"disambiguationData":[OSD([subQ0])],"isStart":false}),makeQuery(id+"FPQ3s8IO0Nq6tfT_4.opExtrude","CAP_FACE",FACE,{"disambiguationData":[OSD([sQuery(id+"Fhg7J0d2X8vjHtq_4.wireOp",EDGE,"c37dfdb1-f1d7-45b2-8367-4b2e48f77e16.bottom"),subQ0,sQuery(id+"Fhg7J0d2X8vjHtq_4.wireOp",EDGE,"c37dfdb1-f1d7-45b2-8367-4b2e48f77e16.left"),sQuery(id+"Fhg7J0d2X8vjHtq_4.wireOp",EDGE,"c37dfdb1-f1d7-45b2-8367-4b2e48f77e16.right")])],"isStart":false})],"blendedInto":[makeQuery(id+"FPQ3s8IO0Nq6tfT_4.opExtrude","CAP_FACE",FACE,{"disambiguationData":[OSD([sQuery(id+"Fhg7J0d2X8vjHtq_4.wireOp",EDGE,"c37dfdb1-f1d7-45b2-8367-4b2e48f77e16.bottom"),subQ0,sQuery(id+"Fhg7J0d2X8vjHtq_4.wireOp",EDGE,"c37dfdb1-f1d7-45b2-8367-4b2e48f77e16.left"),sQuery(id+"Fhg7J0d2X8vjHtq_4.wireOp",EDGE,"c37dfdb1-f1d7-45b2-8367-4b2e48f77e16.right")])],"isStart":false})]});}
            var Q41;
            Q41=makeQuery(id+"FPQ3s8IO0Nq6tfT_4.opExtrude","CAP_EDGE",EDGE,{"disambiguationData":[OSD([sQuery(id+"Fhg7J0d2X8vjHtq_4.wireOp",EDGE,"c37dfdb1-f1d7-45b2-8367-4b2e48f77e16.left")])],"isStart":false});
            var Q42;
            Q42=makeQuery(id+"F19.opExtrude","SWEPT_EDGE",EDGE,{"disambiguationData":[OSD([sQuery(id+"F18.wireOp",EDGE,"E22.top"),sQuery(id+"F18.wireOp",EDGE,"E22.left")])]});
            var Q43;
            Q43=makeQuery(id+"F19.opExtrude","CAP_EDGE",EDGE,{"disambiguationData":[OSD([sQuery(id+"F18.wireOp",EDGE,"E22.top")])],"isStart":false});
            var Q44;
            Q44=makeQuery(id+"F19.opExtrude","SWEPT_EDGE",EDGE,{"disambiguationData":[OSD([sQuery(id+"F18.wireOp",EDGE,"E22.top"),sQuery(id+"F18.wireOp",EDGE,"E22.right")])]});
            chamfer(context, id + "F41", {"entities" : qUnion([Q0, Q1, Q2, Q3, Q4, Q5, Q6, Q7, Q8, Q9, Q10, Q11, Q12, Q13, Q14, Q15, Q16, Q17, Q18, Q19, Q20, Q21, Q22, Q23, Q24, Q25, Q26, Q27, Q28, Q29, Q30, Q31, Q32, Q33, Q34, Q35, Q36, Q37, Q38, Q39, Q40, Q41, Q42, Q43, Q44]), "width" : 10 * mm, "tangentPropagation" : true});
        }
        {
            var Q0;
            Q0=makeQuery(id+"F1.opExtrude","SWEPT_FACE",FACE,{"disambiguationData":[OSD([sQuery(id+"F0.wireOp",EDGE,"E0.bottom")])]});
            var sketch = newSketch(context, id + "F42", { "sketchPlane" : qUnion([Q0])});
            skLineSegment(sketch, "E97", {"start": v(-1013.86, 900) * mm, "end": v(1011.14, 900) * mm});
            skLineSegment(sketch, "E98", {"start": v(1011.14, 900) * mm, "end": v(1011.14, 870) * mm});
            skLineSegment(sketch, "E99", {"start": v(1011.14, 870) * mm, "end": v(-1013.86, 870) * mm});
            skLineSegment(sketch, "E100", {"start": v(-1013.86, 870) * mm, "end": v(-1013.86, 900) * mm});
            skSolve(sketch);
        }
        {
            var Q0;
            Q0=makeQuery(id+"F42.imprint","IMPRINT",FACE,{"disambiguationData":[TD([[makeQuery(id+"F42.imprint","IMPRINT",EDGE,{"derivedFrom":sQuery(id+"F42.wireOp",EDGE,"E97")}),-1.0]])]});
            extrude(context, id + "F43", {"entities" : qUnion([Q0]), "operationType" : NewBodyOperationType.REMOVE, "oppositeDirection" : true, "depth" : 200 * mm});
        }
        {
            var Q0;
            Q0=makeQuery(id+"F27.opExtrude","SWEPT_FACE",FACE,{"disambiguationData":[OSD([sQuery(id+"F26.wireOp",EDGE,"E75"),sQuery(id+"F26.wireOp",EDGE,"E76"),sQuery(id+"F26.wireOp",EDGE,"E86")])]});
            var sketch = newSketch(context, id + "F44", { "sketchPlane" : qUnion([Q0])});
            skLineSegment(sketch, "E101", {"start": v(-6883.86, 900) * mm, "end": v(-4883.86, 900) * mm});
            skLineSegment(sketch, "E102", {"start": v(-4883.86, 900) * mm, "end": v(-4883.86, 870) * mm});
            skLineSegment(sketch, "E103", {"start": v(-4883.86, 870) * mm, "end": v(-6883.86, 870) * mm});
            skLineSegment(sketch, "E104", {"start": v(-6883.86, 870) * mm, "end": v(-6883.86, 900) * mm});
            skSolve(sketch);
        }
        {
            var Q0;
            Q0=qSketchRegion(id+"F44",true);
            extrude(context, id + "F45", {"entities" : qUnion([Q0]), "operationType" : NewBodyOperationType.REMOVE, "oppositeDirection" : true, "depth" : 200 * mm});
        }
        {
            var Q0;
            Q0=makeQuery(id+"F17.boolean.opBoolean","MERGE",FACE,{"derivedFrom":[makeQuery(id+"F13.boolean.opBoolean","MERGE",FACE,{"derivedFrom":[makeQuery(id+"F11.opExtrude","SWEPT_FACE",FACE,{"disambiguationData":[OSD([sQuery(id+"F10.wireOp",EDGE,"E10.top")])]}),makeQuery(id+"F13.opExtrude","SWEPT_FACE",FACE,{"disambiguationData":[OSD([sQuery(id+"F12.wireOp",EDGE,"E12.bottom")])]})]}),makeQuery(id+"F17.opExtrude","SWEPT_FACE",FACE,{"disambiguationData":[OSD([sQuery(id+"F16.wireOp",EDGE,"E14")])]})]});
            var sketch = newSketch(context, id + "F46", { "sketchPlane" : qUnion([Q0])});
            skLineSegment(sketch, "E105.bottom", {"start": v(-1134.15, 896.53) * mm, "end": v(890.85, 896.53) * mm});
            skLineSegment(sketch, "E105.top", {"start": v(-1134.15, 866.53) * mm, "end": v(890.85, 866.53) * mm});
            skLineSegment(sketch, "E105.left", {"start": v(-1134.15, 896.53) * mm, "end": v(-1134.15, 866.53) * mm});
            skLineSegment(sketch, "E105.right", {"start": v(890.85, 896.53) * mm, "end": v(890.85, 866.53) * mm});
            skSolve(sketch);
        }
        {
            var Q0;
            Q0=makeQuery(id+"F46.imprint","IMPRINT",FACE,{"disambiguationData":[TD([[makeQuery(id+"F46.imprint","IMPRINT",EDGE,{"derivedFrom":sQuery(id+"F46.wireOp",EDGE,"E105.bottom")}),-1.0]])]});
            extrude(context, id + "F47", {"entities" : qUnion([Q0]), "operationType" : NewBodyOperationType.REMOVE, "oppositeDirection" : true, "depth" : 180 * mm});
        }
        {
            var Q0;
            Q0=makeQuery(id+"F27.opExtrude","SWEPT_FACE",FACE,{"disambiguationData":[OSD([sQuery(id+"F26.wireOp",EDGE,"E89")])]});
            var sketch = newSketch(context, id + "F48", { "sketchPlane" : qUnion([Q0])});
            skCircle(sketch, "E106", {"center": v(1837.73, 2430) * mm, "radius": 150 * mm});
            skSolve(sketch);
        }
        {
            var Q0;
            Q0=makeQuery(id+"F40.imprint","IMPRINT",FACE,{"disambiguationData":[TD([[makeQuery(id+"F40.imprint","IMPRINT",EDGE,{"derivedFrom":sQuery(id+"F40.wireOp",EDGE,"E96.bottom")}),-1.0]])]});
            extrude(context, id + "F49", {"entities" : qUnion([Q0]), "operationType" : NewBodyOperationType.REMOVE, "oppositeDirection" : true, "depth" : 200 * mm});
        }
        {
            var Q0;
            {var subQ0=sQuery(id+"F0.wireOp",EDGE,"E0.left");var subQ1=sQuery(id+"F0.wireOp",EDGE,"E0.bottom");Q0=makeQuery(id+"F49.boolean.opBoolean","SPLIT",FACE,{"disambiguationData":[TD([makeQuery(id+"F1.opExtrude","SWEPT_FACE",FACE,{"disambiguationData":[OSD([subQ1])]})])],"derivedFrom":makeQuery(id+"F1.opExtrude","SWEPT_FACE",FACE,{"disambiguationData":[OSD([subQ0])]})});}
            var sketch = newSketch(context, id + "F50", { "sketchPlane" : qUnion([Q0])});
            skLineSegment(sketch, "E107.bottom", {"start": v(-3238.73, 900) * mm, "end": v(-1213.73, 900) * mm});
            skLineSegment(sketch, "E107.top", {"start": v(-3238.73, 870) * mm, "end": v(-1213.73, 870) * mm});
            skLineSegment(sketch, "E107.left", {"start": v(-3238.73, 900) * mm, "end": v(-3238.73, 870) * mm});
            skLineSegment(sketch, "E107.right", {"start": v(-1213.73, 900) * mm, "end": v(-1213.73, 870) * mm});
            skSolve(sketch);
        }
        {
            var Q0;
            Q0=makeQuery(id+"F50.imprint","IMPRINT",FACE,{"disambiguationData":[TD([[makeQuery(id+"F50.imprint","IMPRINT",EDGE,{"derivedFrom":sQuery(id+"F50.wireOp",EDGE,"E107.bottom")}),-1.0]])]});
            extrude(context, id + "F51", {"entities" : qUnion([Q0]), "operationType" : NewBodyOperationType.REMOVE, "oppositeDirection" : true, "depth" : 200 * mm});
        }
        {
            var Q0;
            Q0=makeQuery(id+"F17.boolean.opBoolean","MERGE",FACE,{"derivedFrom":[makeQuery(id+"F13.boolean.opBoolean","MERGE",FACE,{"derivedFrom":[makeQuery(id+"F11.opExtrude","SWEPT_FACE",FACE,{"disambiguationData":[OSD([sQuery(id+"F10.wireOp",EDGE,"E10.top")])]}),makeQuery(id+"F13.opExtrude","SWEPT_FACE",FACE,{"disambiguationData":[OSD([sQuery(id+"F12.wireOp",EDGE,"E12.bottom")])]})]}),makeQuery(id+"F17.opExtrude","SWEPT_FACE",FACE,{"disambiguationData":[OSD([sQuery(id+"F16.wireOp",EDGE,"E14")])]})]});
            var sketch = newSketch(context, id + "F52", { "sketchPlane" : qUnion([Q0])});
            skLineSegment(sketch, "E108.left", {"start": v(-1134.15, 841.53) * mm, "end": v(-1134.15, 41.53) * mm});
            skLineSegment(sketch, "E109.bottom", {"start": v(-1134.15, 841.53) * mm, "end": v(890.85, 841.53) * mm});
            skLineSegment(sketch, "E109.top", {"start": v(-1134.15, 41.53) * mm, "end": v(890.85, 41.53) * mm});
            skLineSegment(sketch, "E109.right", {"start": v(890.85, 841.53) * mm, "end": v(890.85, 41.53) * mm});
            skSolve(sketch);
        }
        {
            var Q0;
            Q0=qSketchRegion(id+"F52",true);
            extrude(context, id + "F53", {"entities" : qUnion([Q0]), "operationType" : NewBodyOperationType.REMOVE, "oppositeDirection" : true, "depth" : 200 * mm});
        }
        {
            var Q0;
            Q0=makeQuery(id+"F27.opExtrude","SWEPT_FACE",FACE,{"disambiguationData":[OSD([sQuery(id+"F26.wireOp",EDGE,"E75"),sQuery(id+"F26.wireOp",EDGE,"E76"),sQuery(id+"F26.wireOp",EDGE,"E86")])]});
            var sketch = newSketch(context, id + "F54", { "sketchPlane" : qUnion([Q0])});
            skLineSegment(sketch, "E110.bottom", {"start": v(-6883.86, 845) * mm, "end": v(-4883.86, 845) * mm});
            skLineSegment(sketch, "E110.top", {"start": v(-6883.86, 45) * mm, "end": v(-4883.86, 45) * mm});
            skLineSegment(sketch, "E110.right", {"start": v(-4883.86, 845) * mm, "end": v(-4883.86, 45) * mm});
            skLineSegment(sketch, "E111", {"start": v(-6883.86, 845) * mm, "end": v(-6883.86, 45) * mm});
            skSolve(sketch);
        }
        {
            var Q0;
            Q0=makeQuery(id+"F54.imprint","IMPRINT",FACE,{"disambiguationData":[TD([[makeQuery(id+"F54.imprint","IMPRINT",EDGE,{"derivedFrom":sQuery(id+"F54.wireOp",EDGE,"E110.bottom")}),-1.0]])]});
            extrude(context, id + "F55", {"entities" : qUnion([Q0]), "operationType" : NewBodyOperationType.REMOVE, "oppositeDirection" : true, "depth" : 200 * mm});
        }
        {
            var Q0;
            Q0=sQuery(id+"F48.wireOp",VERTEX,"E106.center");
            var Q1;
            Q1=qCreatedBy(makeId("Top.planeOp"),FACE);
            cPlane(context, id + "F56", {"entities" : qUnion([Q0, Q1]), "cplaneType" : CPlaneType.PLANE_POINT, "offset" : 25 * mm, "width" : 150 * mm, "height" : 150 * mm});
        }
        {
            var Q0;
            Q0=qCreatedBy(id+"F56.planeOp",FACE);
            var sketch = newSketch(context, id + "F57", { "sketchPlane" : qUnion([Q0])});
            skLineSegment(sketch, "E112.0", {"start": v(7471.86, 1987.73) * mm, "end": v(7471.86, 1687.73) * mm});
            skLineSegment(sketch, "E113", {"start": v(7471.86, 1837.73) * mm, "end": v(7521.86, 1837.73) * mm});
            skLineSegment(sketch, "E114", {"start": v(7721.86, 1637.73) * mm, "end": v(7721.86, 1587.73) * mm});
            skPoint(sketch, "E115.visualSharp", {"position": v(7721.86, 1837.73) * mm});
            skArc(sketch, "E115.filletArc", {"start": v(7721.86, 1637.73) * mm, "mid": v(7663.28, 1779.15) * mm, "end": v(7521.86, 1837.73) * mm});
            skSolve(sketch);
        }
        {
            var Q0;
            Q0=qCreatedBy(makeId("Right.planeOp"),FACE);
            var Q1;
            Q1=sQuery(id+"F57.wireOp",VERTEX,"E114.end");
            cPlane(context, id + "F58", {"entities" : qUnion([Q0, Q1]), "cplaneType" : CPlaneType.PLANE_POINT, "offset" : 25 * mm, "width" : 150 * mm, "height" : 150 * mm});
        }
        {
            var Q0;
            Q0=qCreatedBy(id+"F58.planeOp",FACE);
            var sketch = newSketch(context, id + "F59", { "sketchPlane" : qUnion([Q0])});
            skLineSegment(sketch, "E116", {"start": v(1637.73, 2430) * mm, "end": v(887.73, 2430) * mm});
            skLineSegment(sketch, "E117", {"start": v(687.73, 2630) * mm, "end": v(687.73, 8230) * mm});
            skPoint(sketch, "E118.visualSharp", {"position": v(687.73, 2430) * mm});
            skArc(sketch, "E118.filletArc", {"start": v(687.73, 2630) * mm, "mid": v(746.3, 2488.58) * mm, "end": v(887.73, 2430) * mm});
            skPoint(sketch, "E119.0.end.orphan", {"position": v(1837.73, 2430) * mm});
            skPoint(sketch, "E119.0.start.orphan", {"position": v(1637.73, 2430) * mm});
            skSolve(sketch);
        }
        {
            var Q0;
            Q0=makeQuery(id+"F48.imprint","IMPRINT",FACE,{"disambiguationData":[TD([[makeQuery(id+"F48.imprint","IMPRINT",EDGE,{"derivedFrom":sQuery(id+"F48.wireOp",EDGE,"E106")}),1.0]])]});
            var Q1;
            Q1=sQuery(id+"F57.wireOp",EDGE,"E113");
            var Q2;
            Q2=sQuery(id+"F57.wireOp",EDGE,"E115.filletArc");
            var Q3;
            Q3=sQuery(id+"F59.wireOp",EDGE,"E116");
            var Q4;
            Q4=sQuery(id+"F59.wireOp",EDGE,"E118.filletArc");
            var Q5;
            Q5=sQuery(id+"F59.wireOp",EDGE,"E117");
            sweep(context, id + "F60", {"operationType" : NewBodyOperationType.ADD, "profiles" : qUnion([Q0]), "path" : qUnion([Q1, Q2, Q3, Q4, Q5])});
        }
    });
